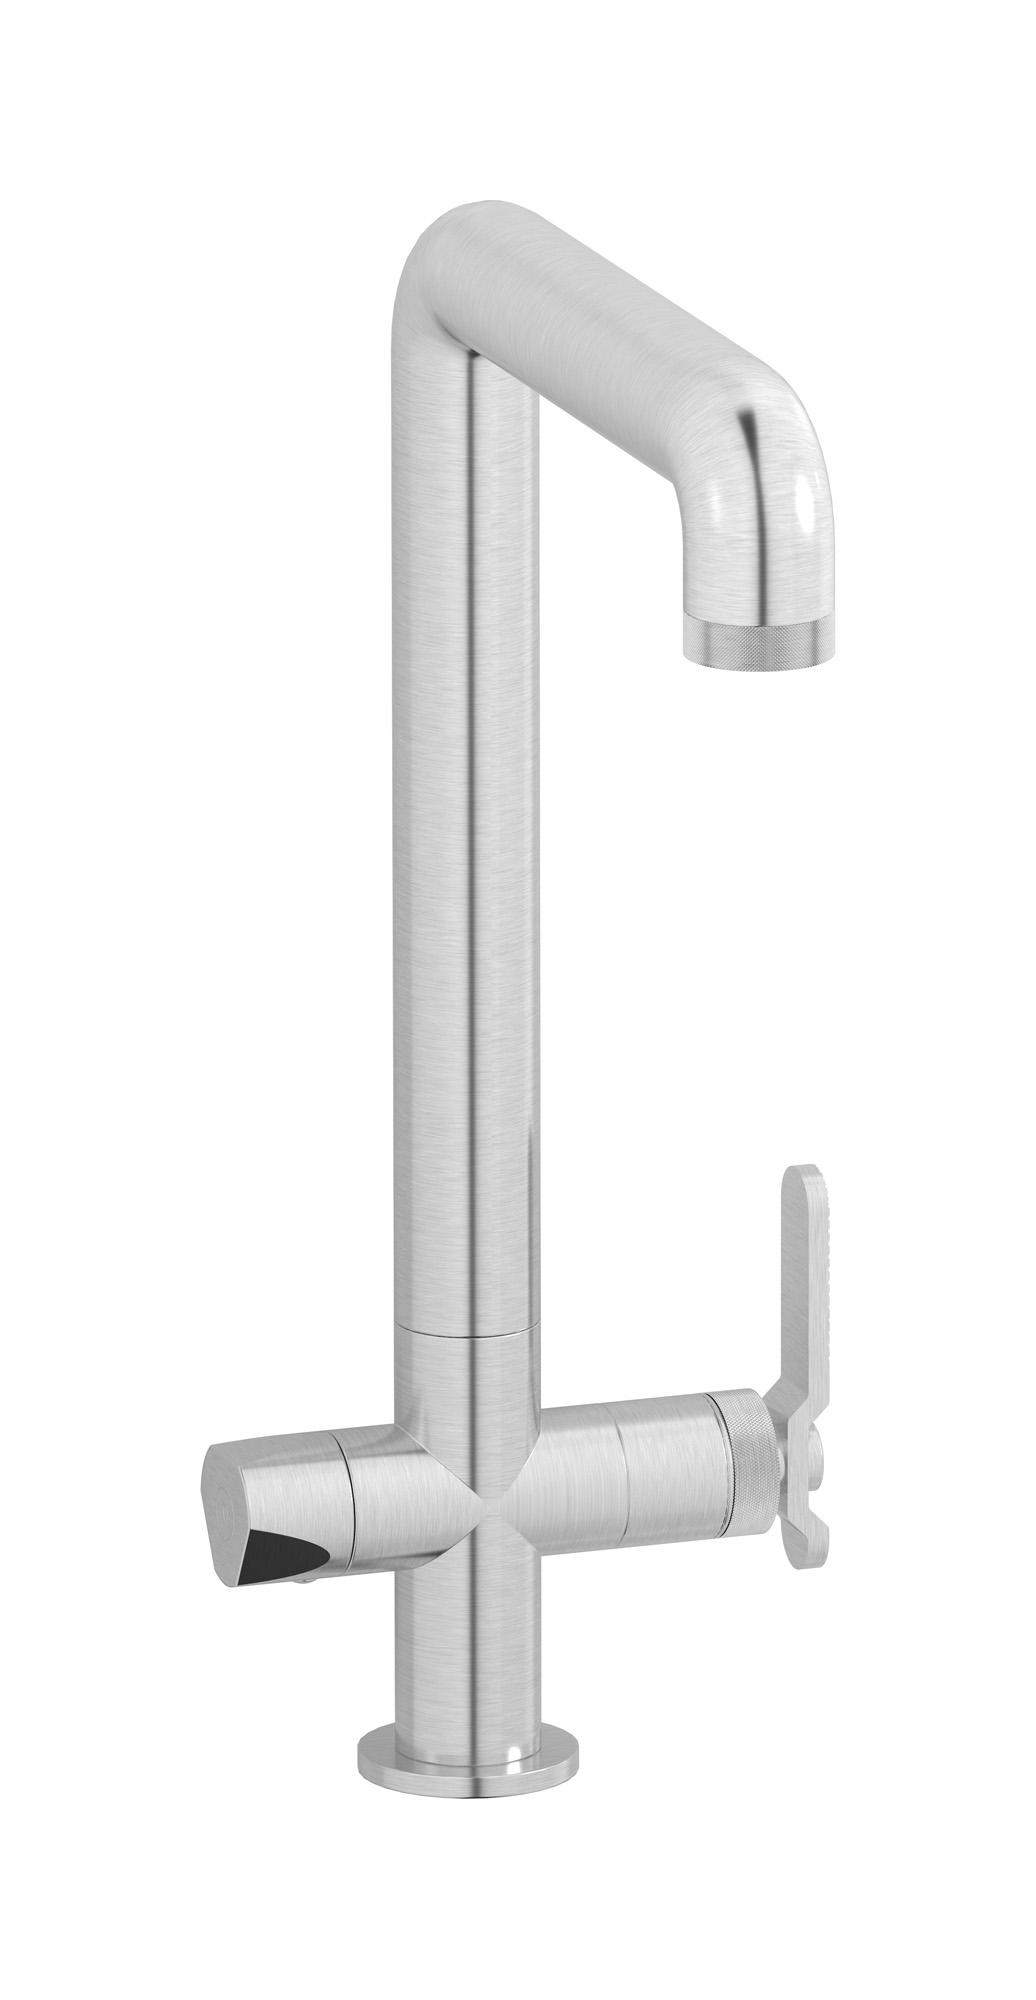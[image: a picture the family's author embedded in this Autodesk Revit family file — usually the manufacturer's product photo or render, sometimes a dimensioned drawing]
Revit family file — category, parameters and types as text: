
# Revit family: B2386
name_source: partatom
category: Apparecchi idraulici
units: mm (PartAtom-declared; Revit-internal decimal feet)

## family parameters
Basato su piano di lavoro = No
Condiviso = No
Mantieni orientamento annotazione = No
Numero OmniClass = 23.45.55.17
Punto di calcolo locali = No
Quota connettore circolare = Usa diametro
Sempre verticale = Sì
Taglio con vuoti quando caricato = No
Tipo di parte = Normale
Titolo OmniClass = Mixing Faucets

## types (6) — shared parameters
Cold water inlet = 10 mm  [stored 0.0328084 ft]
Commenti sul tipo = BOLD Miscelatore monoforo da cucina 2 in 1 per l’erogazione dell’acqua corrente e acqua filtrata naturale a temperatura ambiente
Connessione CW = No
Connessione HW = No
Connessione di scarico = No
Connessione di ventilazione = No
Descrizione = BOLD Miscelatore monoforo da cucina 2 in 1 per l’erogazione dell’acqua corrente e acqua filtrata naturale a temperatura ambiente
Hot water inlet = 10 mm  [stored 0.0328084 ft]
Produttore = IB Rubinetterie S.p.A.
URL = https://www.weareib.it
zero-valued in all types: Prospetto di default

## per-type parameters (varying)
| type | Finishes surface | Immagine tipo | Modello |
| Chrome | IB_Chrome | B2386CC.jpg | B2386CC |
| Brushed Black Chrome | IB_Brushed black chrome | B2386CS.jpg | B2386CS |
| Brushed Pale Gold | IB_brushed pale gold | B2386IS.jpg | B2386IS |
| Matt Black | IB_matt black | B2386NP.jpg | B2386NP |
| Rose Gold | IB_Rose gold | B2386RS.jpg | B2386RS |
| Brushed Nickel | IB_Brushed nickel | B2386SS.jpg | B2386SS |

note: [stored X ft] marks values corroborated as IEEE doubles in the binary element streams (Revit-internal decimal feet)
